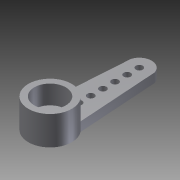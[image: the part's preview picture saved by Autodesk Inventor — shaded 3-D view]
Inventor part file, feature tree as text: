
AUTODESK INVENTOR PART (.ipt)
format: ipt  version: 2011 SP2 (Build 150309200, 309)  size: 133,120 bytes
history: native  units: mm
features: extrude x5, sketch x4, projected_geometry x1
ambient origin geometry x8: Origin, YZ Plane, XZ Plane, XY Plane, X Axis, Y Axis, Z Axis, Center Point
bodies: Solid1 (feature_tree)
feature tree (10):
  sketch  "Sketch1"  dims[d0=6.9mm d1=14.75mm]
  extrude  "Extrusion1"  Depth=14.75mm
  extrude  "Extrusion2"  Depth=1.875mm
  extrude  "Extrusion3"  Depth=5.45mm
  extrude  "Extrusion4"  Depth=1.1mm
  extrude  "Extrusion5"  Depth=1.1mm
  sketch  "Sketch2"  dims[d2=1.875mm d3=1.875mm]
  sketch  "Sketch3"  dims[d4=1.4mm d5=5.45mm]
  sketch  "Sketch4"  dims[d12=1.1mm d13=1.1mm d14=1.1mm d15=1.1mm d16=1.1mm d17=1.1mm d18=1.9298mm d19=1.9298mm d20=1.9298mm d21=1.9298mm d22=1.9298mm d23=1.45mm d24=0.0mm d25=4.6mm d26=0.0mm d27=2.35mm d28=4.6mm d29=0.0mm d30=5.0mm d31=3.0mm d32=0.0mm d33=0.65mm d34=0.0mm]
  projected_geometry  "Projected Loop1"
